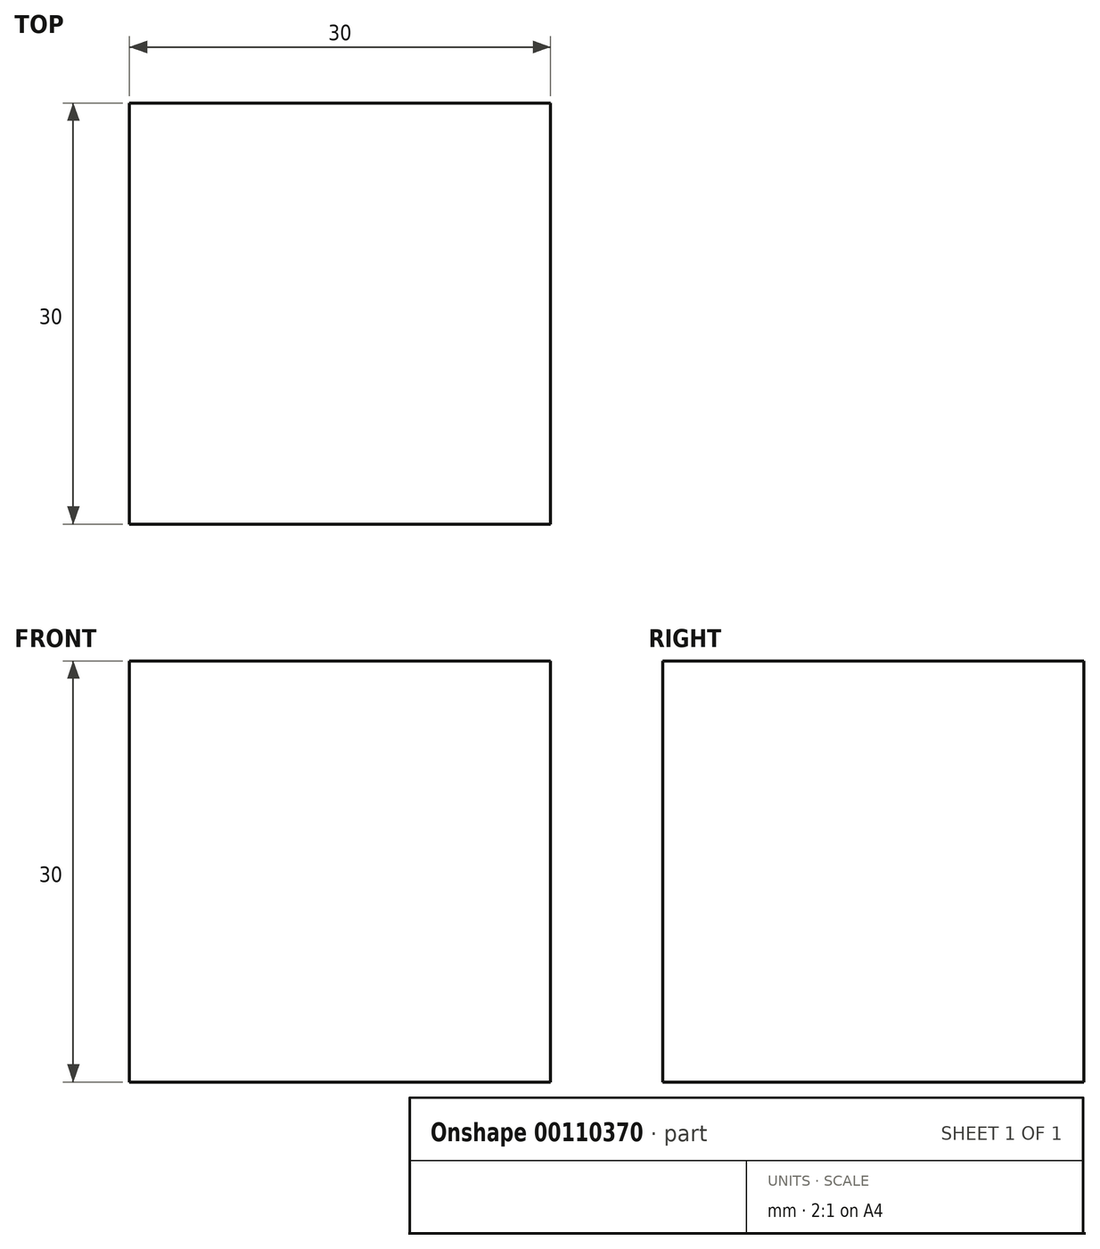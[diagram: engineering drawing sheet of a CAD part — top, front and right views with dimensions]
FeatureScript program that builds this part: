
annotation { "Feature Type Name" : "Feature", "Feature Type Description" : "" }
export const myFeature = defineFeature(function(context is Context, id is Id, definition is map)
    precondition{}
    {
        {
            var Q0;
            Q0=qCreatedBy(makeId("Front.planeOp"),FACE);
            var sketch = newSketch(context, id + "F0", { "sketchPlane" : qUnion([Q0])});
            skLineSegment(sketch, "E0.bottom", {"start": v(-380.53, -358.35) * mm, "end": v(-350.53, -358.35) * mm});
            skLineSegment(sketch, "E0.top", {"start": v(-380.53, -388.35) * mm, "end": v(-350.53, -388.35) * mm});
            skLineSegment(sketch, "E0.left", {"start": v(-380.53, -358.35) * mm, "end": v(-380.53, -388.35) * mm});
            skLineSegment(sketch, "E0.right", {"start": v(-350.53, -358.35) * mm, "end": v(-350.53, -388.35) * mm});
            skSolve(sketch);
        }
        {
            var Q0;
            Q0=makeQuery(id+"F0.imprint","IMPRINT",FACE,{"disambiguationData":[TD([[makeQuery(id+"F0.imprint","IMPRINT",EDGE,{"derivedFrom":sQuery(id+"F0.wireOp",EDGE,"E0.bottom")}),-1.0]])]});
            extrude(context, id + "F1", {"entities" : qUnion([Q0]), "depth" : 30 * mm});
        }
    });
